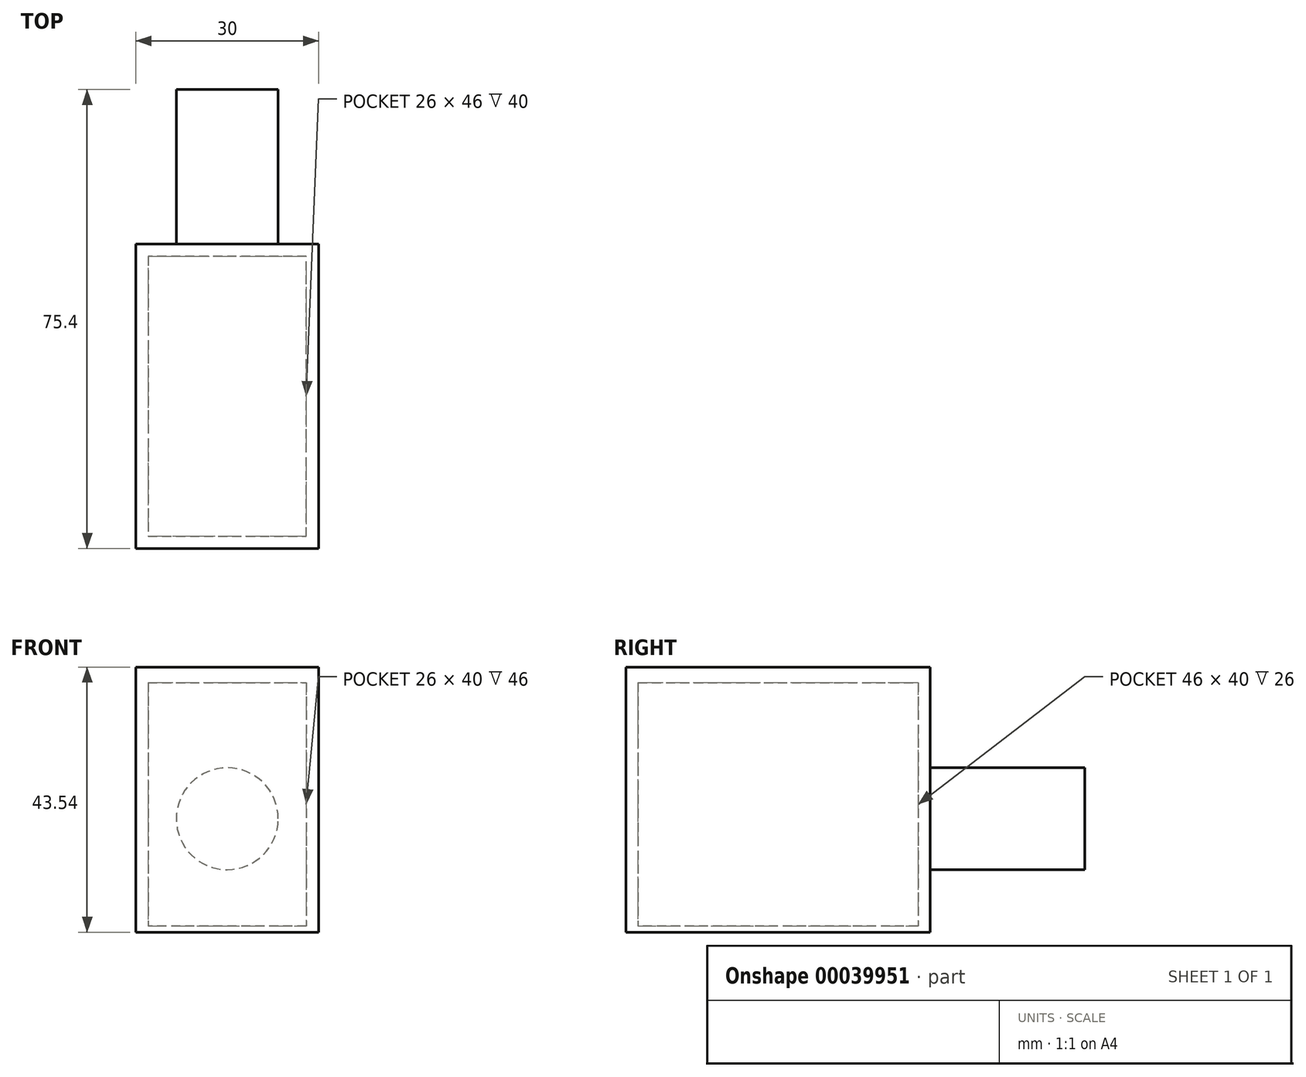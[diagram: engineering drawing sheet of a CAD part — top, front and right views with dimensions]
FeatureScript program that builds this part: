
annotation { "Feature Type Name" : "Feature", "Feature Type Description" : "" }
export const myFeature = defineFeature(function(context is Context, id is Id, definition is map)
    precondition{}
    {
        {
            var Q0;
            Q0=qCreatedBy(makeId("Top.planeOp"),FACE);
            var sketch = newSketch(context, id + "F0", { "sketchPlane" : qUnion([Q0])});
            skLineSegment(sketch, "E0.rect.bottom", {"start": v(-15, 25) * mm, "end": v(15, 25) * mm});
            skLineSegment(sketch, "E0.rect.top", {"start": v(-15, -25) * mm, "end": v(15, -25) * mm});
            skLineSegment(sketch, "E0.rect.left", {"start": v(-15, 25) * mm, "end": v(-15, -25) * mm});
            skLineSegment(sketch, "E0.rect.right", {"start": v(15, 25) * mm, "end": v(15, -25) * mm});
            skPoint(sketch, "E0.rect.middle", {"position": v(0, 0) * mm});
            skSolve(sketch);
        }
        {
            var Q0;
            Q0=makeQuery(id+"F0.imprint","IMPRINT",FACE,{"disambiguationData":[TD([[makeQuery(id+"F0.imprint","IMPRINT",EDGE,{"derivedFrom":sQuery(id+"F0.wireOp",EDGE,"E0.rect.bottom")}),-1.0]])]});
            extrude(context, id + "F1", {"entities" : qUnion([Q0]), "depth" : 1 * mm});
        }
        {
            var Q0;
            Q0=makeQuery(id+"F1.opExtrude","CAP_FACE",FACE,{"disambiguationData":[OSD([sQuery(id+"F0.wireOp",EDGE,"E0.rect.bottom"),sQuery(id+"F0.wireOp",EDGE,"E0.rect.top"),sQuery(id+"F0.wireOp",EDGE,"E0.rect.left"),sQuery(id+"F0.wireOp",EDGE,"E0.rect.right")])],"isStart":false});
            var sketch = newSketch(context, id + "F2", { "sketchPlane" : qUnion([Q0])});
            skLineSegment(sketch, "E1.bottom", {"start": v(-15, 25) * mm, "end": v(-13, 25) * mm});
            skLineSegment(sketch, "E1.top", {"start": v(-15, -25) * mm, "end": v(-13, -25) * mm});
            skLineSegment(sketch, "E1.left", {"start": v(-15, 25) * mm, "end": v(-15, -25) * mm});
            skLineSegment(sketch, "E1.right", {"start": v(-13, 25) * mm, "end": v(-13, -25) * mm});
            skLineSegment(sketch, "E2.bottom", {"start": v(-15, -25) * mm, "end": v(15, -25) * mm});
            skLineSegment(sketch, "E2.top", {"start": v(-15, -23) * mm, "end": v(15, -23) * mm});
            skLineSegment(sketch, "E2.left", {"start": v(-15, -25) * mm, "end": v(-15, -23) * mm});
            skLineSegment(sketch, "E2.right", {"start": v(15, -25) * mm, "end": v(15, -23) * mm});
            skLineSegment(sketch, "E3.bottom", {"start": v(15, -25) * mm, "end": v(13, -25) * mm});
            skLineSegment(sketch, "E3.top", {"start": v(15, 25) * mm, "end": v(13, 25) * mm});
            skLineSegment(sketch, "E3.left", {"start": v(15, -25) * mm, "end": v(15, 25) * mm});
            skLineSegment(sketch, "E3.right", {"start": v(13, -25) * mm, "end": v(13, 25) * mm});
            skLineSegment(sketch, "E4.bottom", {"start": v(15, 25) * mm, "end": v(-15, 25) * mm});
            skLineSegment(sketch, "E4.top", {"start": v(15, 23) * mm, "end": v(-15, 23) * mm});
            skLineSegment(sketch, "E4.left", {"start": v(15, 25) * mm, "end": v(15, 23) * mm});
            skLineSegment(sketch, "E4.right", {"start": v(-15, 25) * mm, "end": v(-15, 23) * mm});
            skSolve(sketch);
        }
        {
            var Q0;
            Q0 = qSketchRegion(id + "F2", true);
            extrude(context, id + "F3", {"entities" : qUnion([Q0]), "operationType" : NewBodyOperationType.ADD, "depth" : 40 * mm});
        }
        {
            var Q0;
            Q0=makeQuery(id+"F3.boolean.opBoolean","MERGE",FACE,{"derivedFrom":[makeQuery(id+"F1.opExtrude","SWEPT_FACE",FACE,{"disambiguationData":[OSD([sQuery(id+"F0.wireOp",EDGE,"E0.rect.bottom")])]}),makeQuery(id+"F3.opExtrude","SWEPT_FACE",FACE,{"disambiguationData":[OSD([sQuery(id+"F2.wireOp",EDGE,"E4.bottom")])]})]});
            var sketch = newSketch(context, id + "F4", { "sketchPlane" : qUnion([Q0])});
            skCircle(sketch, "E5", {"center": v(0, 18.64) * mm, "radius": 8.37 * mm});
            skSolve(sketch);
        }
        {
            var Q0;
            Q0=makeQuery(id+"F3.opExtrude","CAP_FACE",FACE,{"disambiguationData":[OSD([sQuery(id+"F2.wireOp",EDGE,"E1.left"),sQuery(id+"F2.wireOp",EDGE,"E1.right"),sQuery(id+"F2.wireOp",EDGE,"E2.bottom"),sQuery(id+"F2.wireOp",EDGE,"E2.top"),sQuery(id+"F2.wireOp",EDGE,"E2.left"),sQuery(id+"F2.wireOp",EDGE,"E3.bottom"),sQuery(id+"F2.wireOp",EDGE,"E3.left"),sQuery(id+"F2.wireOp",EDGE,"E3.right"),sQuery(id+"F2.wireOp",EDGE,"E4.bottom"),sQuery(id+"F2.wireOp",EDGE,"E4.top"),sQuery(id+"F2.wireOp",EDGE,"E4.left"),sQuery(id+"F2.wireOp",EDGE,"E4.right")])],"isStart":false});
            var sketch = newSketch(context, id + "F5", { "sketchPlane" : qUnion([Q0])});
            skLineSegment(sketch, "E6.bottom", {"start": v(15, -25) * mm, "end": v(-15, -25) * mm});
            skLineSegment(sketch, "E6.top", {"start": v(15, 25) * mm, "end": v(-15, 25) * mm});
            skLineSegment(sketch, "E6.left", {"start": v(15, -25) * mm, "end": v(15, 25) * mm});
            skLineSegment(sketch, "E6.right", {"start": v(-15, -25) * mm, "end": v(-15, 25) * mm});
            skSolve(sketch);
        }
        {
            var Q0;
            Q0 = qSketchRegion(id + "F5", true);
            extrude(context, id + "F6", {"entities" : qUnion([Q0]), "operationType" : NewBodyOperationType.ADD, "depth" : 2.54 * mm});
        }
        {
            var Q0;
            Q0=makeQuery(id+"F4.imprint","IMPRINT",FACE,{"disambiguationData":[TD([[makeQuery(id+"F4.imprint","IMPRINT",EDGE,{"derivedFrom":sQuery(id+"F4.wireOp",EDGE,"E5")}),-1.0]])]});
            var sketch = newSketch(context, id + "F7", { "sketchPlane" : qUnion([Q0])});
            skSolve(sketch);
        }
        {
            var Q0;
            Q0 = qSketchRegion(id + "F7", true);
            var Q1;
            Q1=makeQuery(id+"F4.imprint","IMPRINT",FACE,{"disambiguationData":[TD([[makeQuery(id+"F4.imprint","IMPRINT",EDGE,{"derivedFrom":sQuery(id+"F4.wireOp",EDGE,"E5")}),1.0]])]});
            extrude(context, id + "F8", {"entities" : qUnion([Q0, Q1]), "operationType" : NewBodyOperationType.ADD, "depth" : 25.4 * mm});
        }
    });
